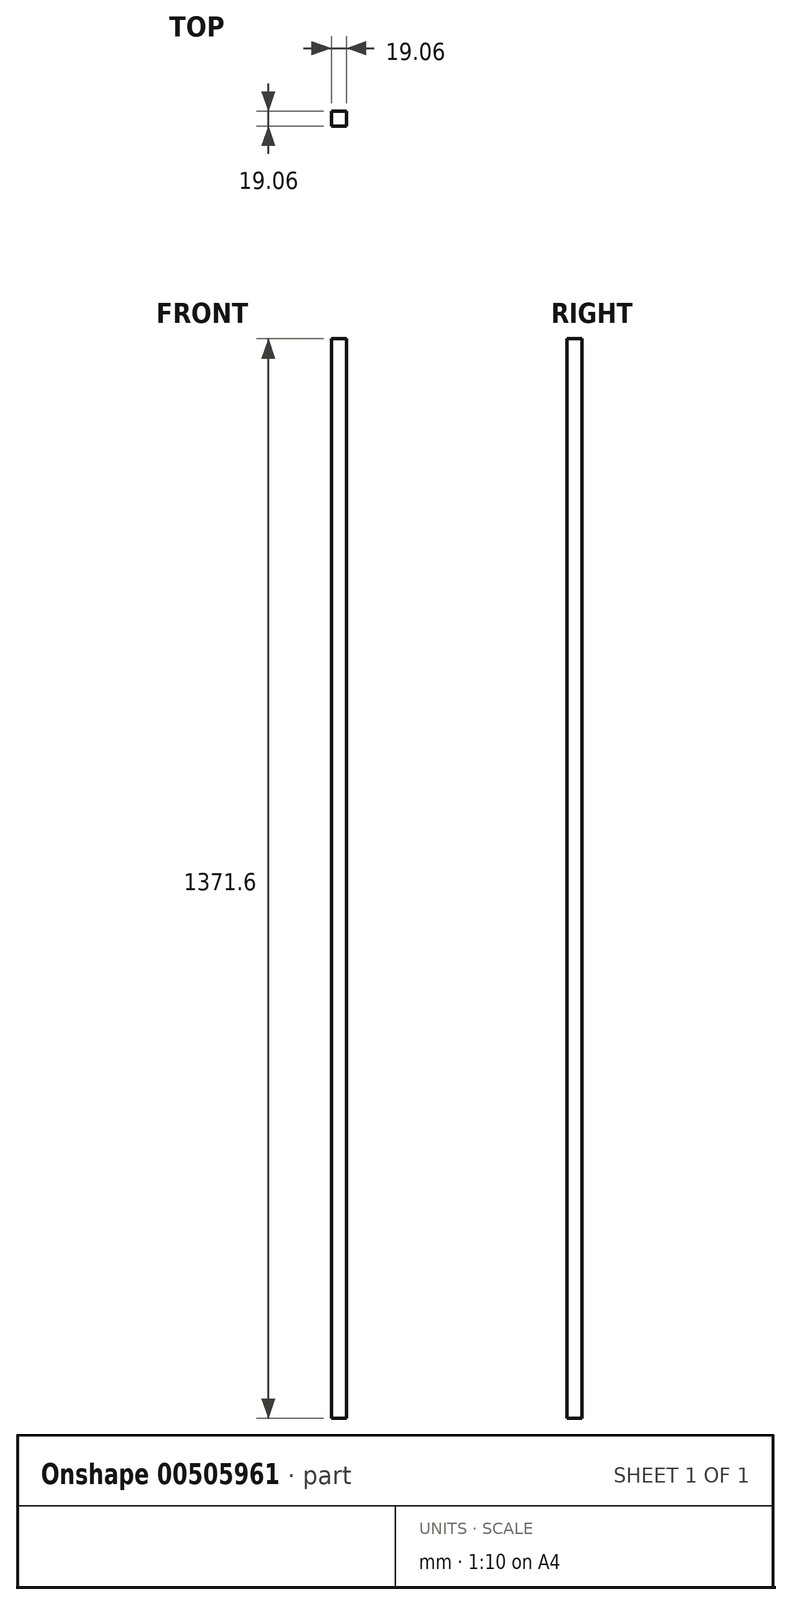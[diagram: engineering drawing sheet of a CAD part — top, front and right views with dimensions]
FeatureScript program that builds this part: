
annotation { "Feature Type Name" : "Feature", "Feature Type Description" : "" }
export const myFeature = defineFeature(function(context is Context, id is Id, definition is map)
    precondition{}
    {
        {
            var Q0;
            Q0=qCreatedBy(makeId("Top.planeOp"),FACE);
            var sketch = newSketch(context, id + "F0", { "sketchPlane" : qUnion([Q0])});
            skLineSegment(sketch, "E0.bottom", {"start": v(-9.52, 9.52) * mm, "end": v(9.53, 9.52) * mm});
            skLineSegment(sketch, "E0.top", {"start": v(-9.53, -9.53) * mm, "end": v(9.52, -9.53) * mm});
            skLineSegment(sketch, "E0.left", {"start": v(-9.52, 9.52) * mm, "end": v(-9.53, -9.53) * mm});
            skLineSegment(sketch, "E0.right", {"start": v(9.53, 9.52) * mm, "end": v(9.52, -9.53) * mm});
            skPoint(sketch, "E0.middle", {"position": v(0, 0) * mm});
            skSolve(sketch);
        }
        {
            var Q0;
            Q0=qSketchRegion(id+"F0",true);
            extrude(context, id + "F1", {"entities" : qUnion([Q0]), "depth" : 1371.6 * mm});
        }
    });
